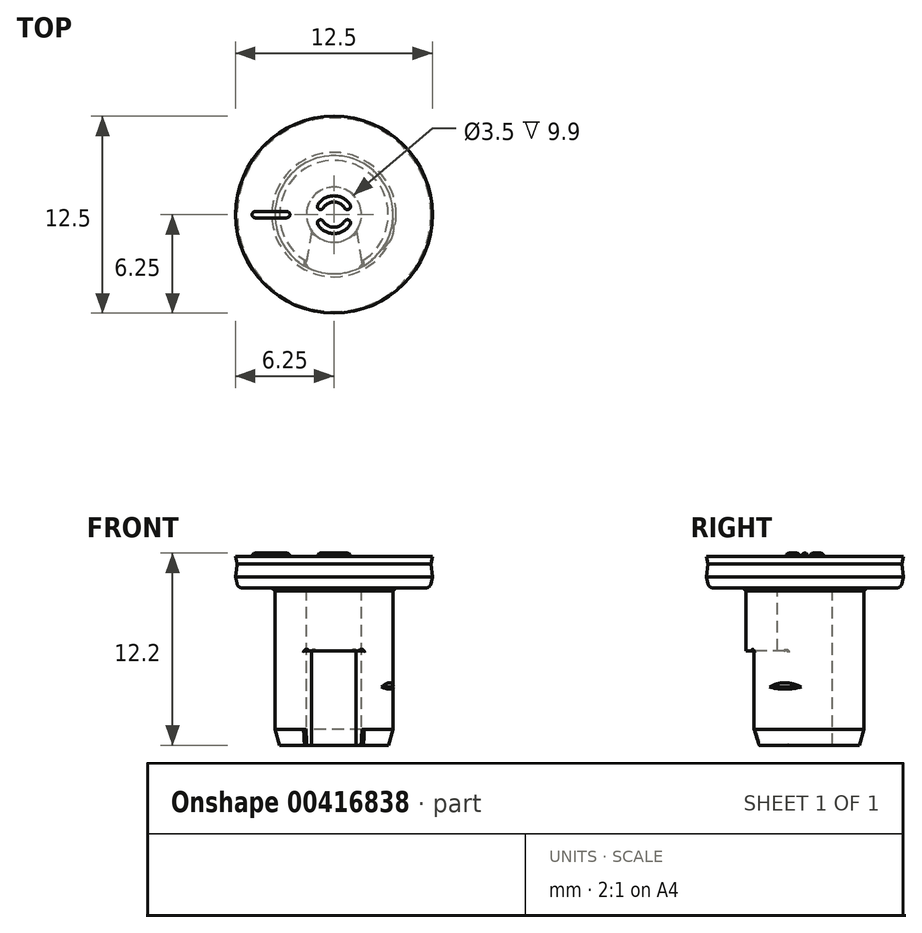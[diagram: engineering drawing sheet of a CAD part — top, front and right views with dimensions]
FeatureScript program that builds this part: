
annotation { "Feature Type Name" : "Feature", "Feature Type Description" : "" }
export const myFeature = defineFeature(function(context is Context, id is Id, definition is map)
    precondition{}
    {
        {
            var Q0;
            Q0=qCreatedBy(makeId("Front.planeOp"),FACE);
            var sketch = newSketch(context, id + "F0", { "sketchPlane" : qUnion([Q0])});
            skLineSegment(sketch, "E0", {"start": v(0, 14.3) * mm, "end": v(0, 0) * mm, "construction": true});
            skLineSegment(sketch, "E1", {"start": v(-1.75, 0) * mm, "end": v(-3.45, 0) * mm});
            skLineSegment(sketch, "E2", {"start": v(-3.75, 1) * mm, "end": v(-3.75, 10) * mm});
            skLineSegment(sketch, "E3", {"start": v(-3.75, 10) * mm, "end": v(-6.1, 10) * mm});
            skLineSegment(sketch, "E4", {"start": v(-6.15, 11.5) * mm, "end": v(-6.25, 12) * mm});
            skLineSegment(sketch, "E5", {"start": v(-6.25, 12) * mm, "end": v(0, 12) * mm});
            skLineSegment(sketch, "E6", {"start": v(0, 12) * mm, "end": v(0, 10) * mm});
            skLineSegment(sketch, "E7", {"start": v(0, 10) * mm, "end": v(-1.75, 10) * mm});
            skLineSegment(sketch, "E8", {"start": v(-1.75, 10) * mm, "end": v(-1.75, 0) * mm});
            skLineSegment(sketch, "E9", {"start": v(-6.15, 11.5) * mm, "end": v(-6.25, 10.7) * mm});
            skLineSegment(sketch, "E10", {"start": v(-6.1, 10) * mm, "end": v(-6.25, 10.7) * mm});
            skLineSegment(sketch, "E11", {"start": v(-3.75, 1) * mm, "end": v(-3.45, 0) * mm});
            skPoint(sketch, "E12.orphan", {"position": v(-3.75, 0) * mm});
            skSolve(sketch);
        }
        {
            var Q0;
            Q0=makeQuery(id+"F0.imprint","IMPRINT",FACE,{"disambiguationData":[TD([[makeQuery(id+"F0.imprint","IMPRINT",EDGE,{"derivedFrom":sQuery(id+"F0.wireOp",EDGE,"E1")}),-1.0]])]});
            var Q1;
            Q1=sQuery(id+"F0.wireOp",EDGE,"Krabe9E8-caii-Rj8K-JC3p-4sixbxrEj6TI");
            var Q2;
            Q2=sQuery(id+"F0.wireOp",EDGE,"E2");
            var Q3;
            Q3=sQuery(id+"F0.wireOp",EDGE,"E8");
            var Q4;
            Q4=sQuery(id+"F0.wireOp",EDGE,"E0");
            revolve(context, id + "F1", {"entities" : qUnion([Q0]), "surfaceEntities" : qUnion([Q1, Q2, Q3]), "axis" : qUnion([Q4]), "revolveType" : RevolveType.FULL});
        }
        {
            var Q0;
            Q0=makeQuery(id+"F1.opRevolve","SWEPT_FACE",FACE,{"disambiguationData":[OSD([sQuery(id+"F0.wireOp",EDGE,"E5")])]});
            var sketch = newSketch(context, id + "F2", { "sketchPlane" : qUnion([Q0])});
            skLineSegment(sketch, "E13.bottom", {"start": v(3, 0.2) * mm, "end": v(5, 0.2) * mm});
            skArc(sketch, "E14", {"start": v(3, 0.2) * mm, "mid": v(2.86, 0.14) * mm, "end": v(2.8, 0) * mm});
            skArc(sketch, "E15", {"start": v(5.2, 0) * mm, "mid": v(5.14, 0.14) * mm, "end": v(5, 0.2) * mm});
            skLineSegment(sketch, "E16", {"start": v(2.13, 0) * mm, "end": v(5.64, 0) * mm, "construction": true});
            skLineSegment(sketch, "E17", {"start": v(2.8, 0) * mm, "end": v(5.2, 0) * mm});
            skSolve(sketch);
        }
        {
            var Q0;
            Q0=makeQuery(id+"F2.imprint","IMPRINT",FACE,{"disambiguationData":[TD([[makeQuery(id+"F2.imprint","IMPRINT",EDGE,{"derivedFrom":sQuery(id+"F2.wireOp",EDGE,"E13.bottom")}),-1.0]])]});
            var Q1;
            Q1=sQuery(id+"F2.wireOp",EDGE,"E16");
            revolve(context, id + "F3", {"operationType" : NewBodyOperationType.ADD, "entities" : qUnion([Q0]), "axis" : qUnion([Q1]), "revolveType" : RevolveType.FULL});
        }
        {
            var Q0;
            Q0=makeQuery(id+"F1.opRevolve","SWEPT_FACE",FACE,{"disambiguationData":[OSD([sQuery(id+"F0.wireOp",EDGE,"E5")])]});
            var sketch = newSketch(context, id + "F4", { "sketchPlane" : qUnion([Q0])});
            skLineSegment(sketch, "E18", {"start": v(-3.22, 1.17) * mm, "end": v(3.16, -1.15) * mm, "construction": true});
            skLineSegment(sketch, "E19", {"start": v(-3.35, -1.22) * mm, "end": v(3.1, 1.13) * mm, "construction": true});
            skLineSegment(sketch, "E20", {"start": v(5.55, 0) * mm, "end": v(0, 0) * mm, "construction": true});
            skArc(sketch, "E21", {"start": v(0.68, 0.42) * mm, "mid": v(0, 0.8) * mm, "end": v(-0.68, 0.42) * mm});
            skArc(sketch, "E22", {"start": v(1.02, 0.63) * mm, "mid": v(0, 1.2) * mm, "end": v(-1.02, 0.63) * mm});
            skCircle(sketch, "E23", {"center": v(-0.85, 0.52) * mm, "radius": 0.2 * mm});
            skCircle(sketch, "E24", {"center": v(0.85, 0.52) * mm, "radius": 0.2 * mm});
            skSolve(sketch);
        }
        {
            var Q0;
            {var subQ0=sQuery(id+"F4.wireOp",EDGE,"E21");Q0=makeQuery(id+"F4.imprint","IMPRINT",FACE,{"disambiguationData":[TD([[makeQuery(id+"F4.imprint","IMPRINT",EDGE,{"derivedFrom":subQ0}),-1.0]])]});}
            var Q1;
            {var subQ0=sQuery(id+"F4.wireOp",EDGE,"E24");var subQ1=makeQuery(id+"F4.imprint","INTERSECT",VERTEX,{"derivedFrom":[sQuery(id+"F4.wireOp",EDGE,"E21"),subQ0]});Q1=makeQuery(id+"F4.imprint","IMPRINT",FACE,{"disambiguationData":[TD([[makeQuery(id+"F4.imprint","IMPRINT",EDGE,{"disambiguationData":[TD([[subQ1,1.0]])],"derivedFrom":subQ0}),1.0]])]});}
            var Q2;
            {var subQ0=sQuery(id+"F4.wireOp",EDGE,"E23");var subQ1=makeQuery(id+"F4.imprint","INTERSECT",VERTEX,{"derivedFrom":[sQuery(id+"F4.wireOp",EDGE,"E21"),subQ0]});Q2=makeQuery(id+"F4.imprint","IMPRINT",FACE,{"disambiguationData":[TD([[makeQuery(id+"F4.imprint","IMPRINT",EDGE,{"disambiguationData":[TD([[subQ1,1.0]])],"derivedFrom":subQ0}),1.0]])]});}
            extrude(context, id + "F5", {"entities" : qUnion([Q0, Q1, Q2]), "operationType" : NewBodyOperationType.ADD, "depth" : .2 * mm});
        }
        {
            var Q0;
            Q0=makeQuery(id+"F5.opExtrude","CAP_FACE",FACE,{"disambiguationData":[OSD([sQuery(id+"F4.wireOp",EDGE,"E21"),sQuery(id+"F4.wireOp",EDGE,"E22"),sQuery(id+"F4.wireOp",EDGE,"E23"),sQuery(id+"F4.wireOp",EDGE,"E24")])],"isStart":false});
            fillet(context, id + "F6", {"entities" : qUnion([Q0]), "radius" : .2 * mm, "tangentPropagation" : true, "allowEdgeOverflow" : false});
        }
        {
            var Q0;
            Q0=makeQuery(id+"F1.opRevolve","SWEPT_BODY",BODY,{"disambiguationData":[OSD([sQuery(id+"F0.wireOp",EDGE,"E1"),sQuery(id+"F0.wireOp",EDGE,"E2"),sQuery(id+"F0.wireOp",EDGE,"E3"),sQuery(id+"F0.wireOp",EDGE,"E4"),sQuery(id+"F0.wireOp",EDGE,"E5"),sQuery(id+"F0.wireOp",EDGE,"E6"),sQuery(id+"F0.wireOp",EDGE,"E7"),sQuery(id+"F0.wireOp",EDGE,"E8"),sQuery(id+"F0.wireOp",EDGE,"E9"),sQuery(id+"F0.wireOp",EDGE,"E10"),sQuery(id+"F0.wireOp",EDGE,"E11")])]});
            var Q1;
            Q1=qCreatedBy(makeId("Front.planeOp"),FACE);
            mirror(context, id + "F7", {"operationType" : NewBodyOperationType.ADD, "entities" : qUnion([Q0]), "mirrorPlane" : qUnion([Q1])});
        }
        {
            var Q0;
            Q0=makeQuery(id+"F1.opRevolve","SWEPT_FACE",FACE,{"disambiguationData":[OSD([sQuery(id+"F0.wireOp",EDGE,"E1")])]});
            var sketch = newSketch(context, id + "F8", { "sketchPlane" : qUnion([Q0])});
            skLineSegment(sketch, "E25", {"start": v(0, -6.29) * mm, "end": v(0, 0) * mm, "construction": true});
            skLineSegment(sketch, "E26", {"start": v(-1.75, -2.97) * mm, "end": v(1.75, -2.97) * mm, "construction": true});
            skLineSegment(sketch, "E27", {"start": v(-1.23, 0) * mm, "end": v(-2.02, -4.51) * mm});
            skLineSegment(sketch, "E28.MirrorCS", {"start": v(1.23, 0) * mm, "end": v(2.02, -4.51) * mm});
            skLineSegment(sketch, "E29", {"start": v(-1.23, 0) * mm, "end": v(1.23, 0) * mm});
            skLineSegment(sketch, "E30", {"start": v(2.02, -4.51) * mm, "end": v(-2.02, -4.51) * mm});
            skSolve(sketch);
        }
        {
            var Q0;
            {var subQ0=sQuery(id+"F8.wireOp",EDGE,"E30");Q0=makeQuery(id+"F8.imprint","IMPRINT",FACE,{"disambiguationData":[TD([[makeQuery(id+"F8.imprint","IMPRINT",EDGE,{"derivedFrom":subQ0}),-1.0]])]});}
            var Q1;
            {var subQ0=sQuery(id+"F8.wireOp",EDGE,"E29");Q1=makeQuery(id+"F8.imprint","IMPRINT",FACE,{"disambiguationData":[TD([[makeQuery(id+"F8.imprint","IMPRINT",EDGE,{"derivedFrom":subQ0}),-1.0]])]});}
            var Q2;
            {var subQ0=sQuery(id+"F8.wireOp",EDGE,"E27");var subQ1=sQuery(id+"F0.wireOp",EDGE,"E1");var subQ2=makeQuery(id+"F1.opRevolve","SWEPT_EDGE",EDGE,{"disambiguationData":[OSD([subQ1,sQuery(id+"F0.wireOp",EDGE,"E11")])]});var subQ3=makeQuery(id+"F8.imprint","INTERSECT",VERTEX,{"derivedFrom":[subQ2,subQ0]});Q2=makeQuery(id+"F8.imprint","IMPRINT",FACE,{"disambiguationData":[TD([[makeQuery(id+"F8.imprint","IMPRINT",EDGE,{"disambiguationData":[TD([[subQ3,1.0]])],"derivedFrom":subQ0}),1.0]])]});}
            var Q3;
            Q3=sQuery(id+"F8.wireOp",EDGE,"E26");
            extrude(context, id + "F9", {"entities" : qUnion([Q0, Q1, Q2]), "operationType" : NewBodyOperationType.REMOVE, "surfaceEntities" : qUnion([Q3]), "oppositeDirection" : true, "depth" : 6 * mm});
        }
        {
            var Q0;
            Q0=makeQuery(id+"F1.opRevolve","SWEPT_EDGE",EDGE,{"disambiguationData":[OSD([sQuery(id+"F0.wireOp",EDGE,"E3"),sQuery(id+"F0.wireOp",EDGE,"E10")])]});
            fillet(context, id + "F10", {"entities" : qUnion([Q0]), "radius" : .3 * mm, "tangentPropagation" : true, "allowEdgeOverflow" : false});
        }
        {
            var Q0;
            Q0=makeQuery(id+"F1.opRevolve","SWEPT_BODY",BODY,{"disambiguationData":[OSD([sQuery(id+"F0.wireOp",EDGE,"E1"),sQuery(id+"F0.wireOp",EDGE,"E2"),sQuery(id+"F0.wireOp",EDGE,"E3"),sQuery(id+"F0.wireOp",EDGE,"E4"),sQuery(id+"F0.wireOp",EDGE,"E5"),sQuery(id+"F0.wireOp",EDGE,"E6"),sQuery(id+"F0.wireOp",EDGE,"E7"),sQuery(id+"F0.wireOp",EDGE,"E8"),sQuery(id+"F0.wireOp",EDGE,"E9"),sQuery(id+"F0.wireOp",EDGE,"E10"),sQuery(id+"F0.wireOp",EDGE,"E11")])]});
            var Q1;
            Q1=makeQuery(id+"F1.opRevolve","SWEPT_EDGE",EDGE,{"disambiguationData":[OSD([sQuery(id+"F0.wireOp",EDGE,"E4"),sQuery(id+"F0.wireOp",EDGE,"E5")])]});
            transform(context, id + "F11", {"entities" : qUnion([Q0]), "transformType" : TransformType.ROTATION, "transformAxis" : qUnion([Q1]), "angle" : 180 * degree, "makeCopy" : false});
        }
        {
            var Q0;
            Q0=qCreatedBy(makeId("Top.planeOp"),FACE);
            cPlane(context, id + "F12", {"entities" : qUnion([Q0]), "cplaneType" : CPlaneType.OFFSET, "offset" : 3.7 * mm, "width" : 150 * mm, "height" : 150 * mm});
        }
        {
            var Q0;
            Q0=qCreatedBy(id+"F12.planeOp",FACE);
            var sketch = newSketch(context, id + "F13", { "sketchPlane" : qUnion([Q0])});
            skLineSegment(sketch, "E31", {"start": v(-7.22, 2.63) * mm, "end": v(8.3, -3.02) * mm, "construction": true});
            skLineSegment(sketch, "E32", {"start": v(-7.37, -2.68) * mm, "end": v(8.39, 3.05) * mm, "construction": true});
            skLineSegment(sketch, "E33", {"start": v(-9.7, 0) * mm, "end": v(10.27, 0) * mm, "construction": true});
            skArc(sketch, "E34.0", {"start": v(3, -2.24) * mm, "mid": v(3.52, -1.28) * mm, "end": v(3.74, -0.21) * mm});
            skArc(sketch, "E35", {"start": v(3, -2.24) * mm, "mid": v(3.72, -1.35) * mm, "end": v(3.74, -0.21) * mm});
            skPoint(sketch, "E36.orphan", {"position": v(1.8, -3.29) * mm});
            skArc(sketch, "E37.trimOffspring", {"start": v(3.52, 1.28) * mm, "mid": v(-2.44, 2.85) * mm, "end": v(-1.8, -3.29) * mm});
            skSolve(sketch);
        }
        {
            var Q0;
            {var subQ0=sQuery(id+"F13.wireOp",EDGE,"E35");Q0=makeQuery(id+"F13.imprint","IMPRINT",FACE,{"disambiguationData":[TD([[makeQuery(id+"F13.imprint","IMPRINT",EDGE,{"derivedFrom":subQ0}),1.0]])]});}
            extrude(context, id + "F14", {"entities" : qUnion([Q0]), "operationType" : NewBodyOperationType.ADD, "flatOperationType" : FlatOperationType.REMOVE, "offsetDistance" : 25 * mm, "depth" : .25 * mm, "hasSecondDirection" : true, "secondDirectionOppositeDirection" : true, "secondDirectionDepth" : .20 * mm, "domain" : OperationDomain.MODEL});
        }
        {
            var Q0;
            Q0=makeQuery(id+"F14.opExtrude","CAP_EDGE",EDGE,{"disambiguationData":[OSD([sQuery(id+"F13.wireOp",EDGE,"E35")])],"isStart":false});
            chamfer(context, id + "F15", {"entities" : qUnion([Q0]), "chamferType" : ChamferType.TWO_OFFSETS, "width1" : .19 * mm, "oppositeDirection" : false, "width2" : .25 * mm, "tangentPropagation" : true});
        }
        {
            var Q0;
            Q0=makeQuery(id+"F14.opExtrude","CAP_EDGE",EDGE,{"disambiguationData":[OSD([sQuery(id+"F13.wireOp",EDGE,"E35")])],"isStart":true});
            chamfer(context, id + "F16", {"entities" : qUnion([Q0]), "chamferType" : ChamferType.TWO_OFFSETS, "width1" : .2 * mm, "oppositeDirection" : false, "width2" : .3 * mm, "tangentPropagation" : true});
        }
        {
            var Q0;
            Q0=makeQuery(id+"F1.opRevolve","SWEPT_EDGE",EDGE,{"disambiguationData":[OSD([sQuery(id+"F0.wireOp",EDGE,"E2"),sQuery(id+"F0.wireOp",EDGE,"E3")])]});
            chamfer(context, id + "F17", {"entities" : qUnion([Q0]), "width" : .2 * mm, "tangentPropagation" : true});
        }
        {
            var Q0;
            Q0=makeQuery(id+"F9.boolean.opBoolean","COPY",FACE,{"derivedFrom":makeQuery(id+"F9.opExtrude","SWEPT_FACE",FACE,{"disambiguationData":[OSD([sQuery(id+"F8.wireOp",EDGE,"E27")])]})});
            var Q1;
            Q1=makeQuery(id+"F9.boolean.opBoolean","COPY",FACE,{"derivedFrom":makeQuery(id+"F9.opExtrude","SWEPT_FACE",FACE,{"disambiguationData":[OSD([sQuery(id+"F8.wireOp",EDGE,"E28.MirrorCS")])]})});
            var Q2;
            Q2=makeQuery(id+"F1.opRevolve","SWEPT_EDGE",EDGE,{"disambiguationData":[OSD([sQuery(id+"F0.wireOp",EDGE,"E7"),sQuery(id+"F0.wireOp",EDGE,"E8")])]});
            fillet(context, id + "F18", {"entities" : qUnion([Q0, Q1, Q2]), "radius" : .1 * mm, "tangentPropagation" : true, "allowEdgeOverflow" : false});
        }
    });
